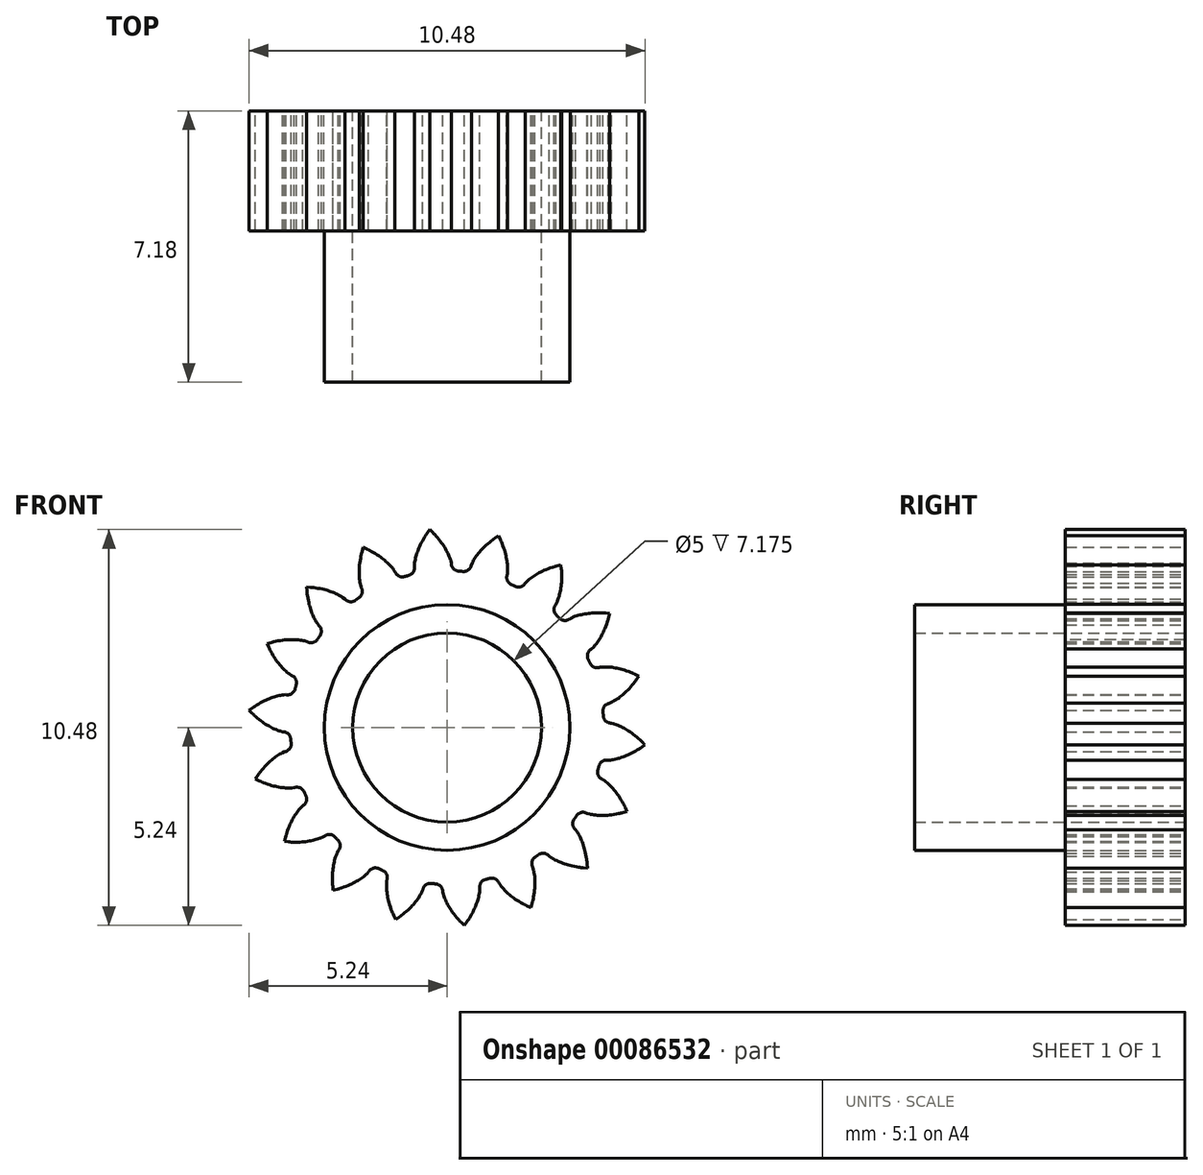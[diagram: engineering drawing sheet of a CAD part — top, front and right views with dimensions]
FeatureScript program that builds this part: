
annotation { "Feature Type Name" : "Feature", "Feature Type Description" : "" }
export const myFeature = defineFeature(function(context is Context, id is Id, definition is map)
    precondition{}
    {
        {
            assignVariable(context, id + "F0", {"name" : "Teeth", "anyValue" : 18});
        }
        {
            var Q0;
            Q0=qCreatedBy(makeId("Front.planeOp"),FACE);
            var sketch = newSketch(context, id + "F1", { "sketchPlane" : qUnion([Q0])});
            skCircle(sketch, "E0", {"center": v(0, 0) * mm, "radius": 4.24 * mm, "construction": true});
            skLineSegment(sketch, "E1", {"start": v(0, 0) * mm, "end": v(-0.2, 4.24) * mm, "construction": true});
            skLineSegment(sketch, "E2", {"start": v(0, 0) * mm, "end": v(-0.52, 4.21) * mm, "construction": true});
            skLineSegment(sketch, "E3", {"start": v(0, 0) * mm, "end": v(-0.84, 4.16) * mm, "construction": true});
            skLineSegment(sketch, "E4", {"start": v(-0.84, 4.16) * mm, "end": v(0.11, 4.35) * mm, "construction": true});
            skLineSegment(sketch, "E5", {"start": v(0, 0) * mm, "end": v(-1.15, 4.08) * mm, "construction": true});
            skLineSegment(sketch, "E6", {"start": v(-1.15, 4.08) * mm, "end": v(0.1, 4.43) * mm, "construction": true});
            skLineSegment(sketch, "E7", {"start": v(-0.84, 4.16) * mm, "end": v(-0.52, 4.21) * mm, "construction": true});
            skLineSegment(sketch, "E8", {"start": v(-1.15, 4.08) * mm, "end": v(-0.84, 4.16) * mm, "construction": true});
            skLineSegment(sketch, "E9", {"start": v(-0.84, 4.16) * mm, "end": v(-0.2, 4.24) * mm, "construction": true});
            skLineSegment(sketch, "E10", {"start": v(-1.15, 4.08) * mm, "end": v(-0.2, 4.24) * mm, "construction": true});
            skLineSegment(sketch, "E11", {"start": v(0, 0) * mm, "end": v(-2.05, 3.72) * mm, "construction": true});
            skLineSegment(sketch, "E12", {"start": v(-2.05, 3.72) * mm, "end": v(-0.09, 4.8) * mm, "construction": true});
            skLineSegment(sketch, "E13", {"start": v(0, 0) * mm, "end": v(-1.76, 3.86) * mm, "construction": true});
            skLineSegment(sketch, "E14", {"start": v(-1.76, 3.86) * mm, "end": v(0, 4.66) * mm, "construction": true});
            skLineSegment(sketch, "E15", {"start": v(0, 0) * mm, "end": v(-1.46, 3.98) * mm, "construction": true});
            skLineSegment(sketch, "E16", {"start": v(-1.46, 3.98) * mm, "end": v(0.05, 4.54) * mm, "construction": true});
            skLineSegment(sketch, "E17", {"start": v(-1.46, 3.98) * mm, "end": v(-1.15, 4.08) * mm, "construction": true});
            skLineSegment(sketch, "E18", {"start": v(-1.46, 3.98) * mm, "end": v(-1.76, 3.86) * mm, "construction": true});
            skLineSegment(sketch, "E19", {"start": v(-1.76, 3.86) * mm, "end": v(-2.05, 3.72) * mm, "construction": true});
            skLineSegment(sketch, "E20", {"start": v(-1.46, 3.98) * mm, "end": v(-0.2, 4.24) * mm, "construction": true});
            skLineSegment(sketch, "E21", {"start": v(-1.76, 3.86) * mm, "end": v(-0.2, 4.24) * mm, "construction": true});
            skLineSegment(sketch, "E22", {"start": v(-2.05, 3.72) * mm, "end": v(-0.2, 4.24) * mm, "construction": true});
            skLineSegment(sketch, "E23", {"start": v(0, 0) * mm, "end": v(-2.59, 3.36) * mm, "construction": true});
            skLineSegment(sketch, "E24", {"start": v(-2.59, 3.36) * mm, "end": v(-0.32, 5.1) * mm, "construction": true});
            skLineSegment(sketch, "E25", {"start": v(0, 0) * mm, "end": v(-2.84, 3.15) * mm, "construction": true});
            skLineSegment(sketch, "E26", {"start": v(-2.84, 3.15) * mm, "end": v(-0.49, 5.27) * mm, "construction": true});
            skLineSegment(sketch, "E27", {"start": v(0, 0) * mm, "end": v(-3.07, 2.93) * mm, "construction": true});
            skLineSegment(sketch, "E28", {"start": v(0, 0) * mm, "end": v(-2.33, 3.55) * mm, "construction": true});
            skLineSegment(sketch, "E29", {"start": v(-2.33, 3.55) * mm, "end": v(-0.2, 4.95) * mm, "construction": true});
            skLineSegment(sketch, "E30", {"start": v(-2.05, 3.72) * mm, "end": v(-2.33, 3.55) * mm, "construction": true});
            skLineSegment(sketch, "E31", {"start": v(-2.33, 3.55) * mm, "end": v(-2.59, 3.36) * mm, "construction": true});
            skLineSegment(sketch, "E32", {"start": v(-2.59, 3.36) * mm, "end": v(-2.84, 3.15) * mm, "construction": true});
            skLineSegment(sketch, "E33", {"start": v(-2.84, 3.15) * mm, "end": v(-3.07, 2.93) * mm, "construction": true});
            skLineSegment(sketch, "E34", {"start": v(-0.2, 4.24) * mm, "end": v(-2.33, 3.55) * mm, "construction": true});
            skLineSegment(sketch, "E35", {"start": v(-0.2, 4.24) * mm, "end": v(-2.59, 3.36) * mm, "construction": true});
            skLineSegment(sketch, "E36", {"start": v(-0.2, 4.24) * mm, "end": v(-2.84, 3.15) * mm, "construction": true});
            skLineSegment(sketch, "E37", {"start": v(-0.2, 4.24) * mm, "end": v(-3.07, 2.93) * mm, "construction": true});
            skCircle(sketch, "E38", {"center": v(0, 0) * mm, "radius": 4.76 * mm, "construction": true});
            skCircle(sketch, "E39", {"center": v(0, 0) * mm, "radius": 5.3 * mm});
            skPoint(sketch, "E40", {"position": v(0, 4.76) * mm});
            skLineSegment(sketch, "E41", {"start": v(0, 0) * mm, "end": v(-0.75, 8.57) * mm, "construction": true});
            skPoint(sketch, "E42.MirrorP", {"position": v(-0.83, 4.7) * mm});
            skLineSegment(sketch, "E43", {"start": v(-0.83, 4.7) * mm, "end": v(0, 0) * mm, "construction": true});
            skLineSegment(sketch, "E44", {"start": v(0, 0) * mm, "end": v(0, 4.76) * mm, "construction": true});
            skLineSegment(sketch, "E45", {"start": v(-0.52, 4.21) * mm, "end": v(-0.2, 4.24) * mm, "construction": true});
            skLineSegment(sketch, "E46", {"start": v(0.11, 4.35) * mm, "end": v(0.1, 4.43) * mm, "construction": true});
            skLineSegment(sketch, "E47", {"start": v(0, 0) * mm, "end": v(0, 10.19) * mm, "construction": true});
            skCircle(sketch, "E48", {"center": v(0, 0) * mm, "radius": 4.15 * mm});
            skSolve(sketch);
        }
        {
            var Q0;
            Q0=qCreatedBy(makeId("Front.planeOp"),FACE);
            var sketch = newSketch(context, id + "F2", { "sketchPlane" : qUnion([Q0])});
            skCircle(sketch, "E49.0", {"center": v(0, 0) * mm, "radius": 4.76 * mm, "construction": true});
            skPoint(sketch, "E50.0", {"position": v(-0.49, 5.27) * mm});
            skPoint(sketch, "E50.1", {"position": v(-0.32, 5.1) * mm});
            skPoint(sketch, "E50.2", {"position": v(-0.2, 4.95) * mm});
            skPoint(sketch, "E50.3", {"position": v(-0.09, 4.8) * mm});
            skPoint(sketch, "E50.4", {"position": v(0, 4.66) * mm});
            skPoint(sketch, "E50.6", {"position": v(0.1, 4.43) * mm});
            skPoint(sketch, "E50.7", {"position": v(0.11, 4.35) * mm});
            skPoint(sketch, "E50.8", {"position": v(0.05, 4.54) * mm});
            skLineSegment(sketch, "E51.0", {"start": v(0, 0) * mm, "end": v(-0.75, 8.57) * mm, "construction": true});
            skFitSpline(sketch, "E52", {"points": [v(-0.49, 5.27) * mm, v(-0.32, 5.1) * mm, v(-0.2, 4.95) * mm, v(-0.09, 4.8) * mm, v(0, 4.66) * mm, v(0.05, 4.54) * mm, v(0.1, 4.43) * mm, v(0.11, 4.35) * mm], "startDerivative": vector(2.81, -2.8) * mm, "endDerivative": vector(0.65, -2.34) * mm});
            skFitSpline(sketch, "E53.MirrorCS", {"points": [v(-0.43, 5.27) * mm, v(-0.57, 5.09) * mm, v(-0.67, 4.9) * mm, v(-0.75, 4.74) * mm, v(-0.8, 4.6) * mm, v(-0.84, 4.46) * mm, v(-0.86, 4.35) * mm, v(-0.87, 4.27) * mm], "startDerivative": vector(-2.28, -3.25) * mm, "endDerivative": vector(-0.24, -2.42) * mm});
            skCircle(sketch, "E54", {"center": v(0, 0) * mm, "radius": 2.5 * mm});
            skCircle(sketch, "E55.0", {"center": v(0, 0) * mm, "radius": 4.15 * mm});
            skArc(sketch, "E56", {"start": v(-0.49, 5.27) * mm, "mid": v(0.46, -5.27) * mm, "end": v(-0.43, 5.27) * mm});
            skLineSegment(sketch, "E57", {"start": v(-0.87, 4.27) * mm, "end": v(0, 0) * mm});
            skLineSegment(sketch, "E58", {"start": v(0, 0) * mm, "end": v(0.11, 4.35) * mm});
            skSolve(sketch);
        }
        {
            var Q0;
            {var subQ1=sQuery(id+"F2.wireOp",EDGE,"E52");var subQ9=sQuery(id+"F2.wireOp",EDGE,"rA0usyOi-Jm6w-jZNR-JSDv-ujEcH4bsm2Ol");var subQ11=makeQuery(id+"F2.imprint","INTERSECT",VERTEX,{"derivedFrom":[subQ1,subQ9]});Q0=makeQuery(id+"F2.imprint","IMPRINT",FACE,{"disambiguationData":[TD([[makeQuery(id+"F2.imprint","IMPRINT",EDGE,{"disambiguationData":[TD([[subQ11,1.0]])],"derivedFrom":subQ1}),-1.0]])]});}
            var Q1;
            {var subQ0=sQuery(id+"F2.wireOp",EDGE,"QqPcIgQ4-TZE6-73E5-WQaq-ugCT5JtziKyn");var subQ1=sQuery(id+"F2.wireOp",EDGE,"90be38e0-c88f-493d-85a8-1201295b9109.0");var subQ2=makeQuery(id+"F2.imprint","INTERSECT",VERTEX,{"derivedFrom":[subQ1,subQ0]});Q1=makeQuery(id+"F2.imprint","IMPRINT",FACE,{"disambiguationData":[TD([[makeQuery(id+"F2.imprint","IMPRINT",EDGE,{"disambiguationData":[TD([[subQ2,1.0]])],"derivedFrom":subQ1}),1.0]])]});}
            var Q2;
            {var subQ0=sQuery(id+"F2.wireOp",EDGE,"QqPcIgQ4-TZE6-73E5-WQaq-ugCT5JtziKyn");var subQ1=sQuery(id+"F2.wireOp",EDGE,"90be38e0-c88f-493d-85a8-1201295b9109.0");var subQ2=makeQuery(id+"F2.imprint","INTERSECT",VERTEX,{"derivedFrom":[subQ1,subQ0]});Q2=makeQuery(id+"F2.imprint","IMPRINT",FACE,{"disambiguationData":[TD([[makeQuery(id+"F2.imprint","IMPRINT",EDGE,{"disambiguationData":[TD([[subQ2,-1.0]])],"derivedFrom":subQ1}),1.0]])]});}
            var Q3;
            {var subQ1=sQuery(id+"F2.wireOp",EDGE,"E52");var subQ8=sQuery(id+"F2.wireOp",EDGE,"b861a5ab-cd51-40f1-92ab-cea0f5fe0d4d.1");var subQ11=makeQuery(id+"F2.imprint","INTERSECT",VERTEX,{"derivedFrom":[subQ1,subQ8]});Q3=makeQuery(id+"F2.imprint","IMPRINT",FACE,{"disambiguationData":[TD([[makeQuery(id+"F2.imprint","IMPRINT",EDGE,{"disambiguationData":[TD([[subQ11,1.0]])],"derivedFrom":subQ1}),-1.0]])]});}
            var Q4;
            {var subQ0=sQuery(id+"F2.wireOp",EDGE,"b861a5ab-cd51-40f1-92ab-cea0f5fe0d4d.0");var subQ1=sQuery(id+"F2.wireOp",EDGE,"E54");var subQ2=makeQuery(id+"F2.imprint","INTERSECT",VERTEX,{"derivedFrom":[subQ1,subQ0]});Q4=makeQuery(id+"F2.imprint","IMPRINT",FACE,{"disambiguationData":[TD([[makeQuery(id+"F2.imprint","IMPRINT",EDGE,{"disambiguationData":[TD([[subQ2,-1.0]])],"derivedFrom":subQ1}),-1.0]])]});}
            var Q5;
            {var subQ0=sQuery(id+"F2.wireOp",EDGE,"b861a5ab-cd51-40f1-92ab-cea0f5fe0d4d.0");var subQ1=sQuery(id+"F2.wireOp",EDGE,"E54");var subQ2=makeQuery(id+"F2.imprint","INTERSECT",VERTEX,{"derivedFrom":[subQ1,subQ0]});Q5=makeQuery(id+"F2.imprint","IMPRINT",FACE,{"disambiguationData":[TD([[makeQuery(id+"F2.imprint","IMPRINT",EDGE,{"disambiguationData":[TD([[subQ2,1.0]])],"derivedFrom":subQ1}),-1.0]])]});}
            extrude(context, id + "F3", {"entities" : qUnion([Q0, Q1, Q2, Q3, Q4, Q5]), "depth" : 3.17 * mm});
        }
        {
            var Q0;
            Q0=makeQuery(id+"F3.opExtrude","SWEPT_EDGE",EDGE,{"disambiguationData":[OSD([sQuery(id+"F2.wireOp",EDGE,"b861a5ab-cd51-40f1-92ab-cea0f5fe0d4d.1"),sQuery(id+"F2.wireOp",EDGE,"E55.0")])]});
            var Q1;
            Q1=makeQuery(id+"F3.opExtrude","SWEPT_EDGE",EDGE,{"disambiguationData":[OSD([sQuery(id+"F2.wireOp",EDGE,"b861a5ab-cd51-40f1-92ab-cea0f5fe0d4d.0"),sQuery(id+"F2.wireOp",EDGE,"E55.0")])]});
            fillet(context, id + "F4", {"entities" : qUnion([Q0, Q1]), "radius" : 0.2 * mm, "tangentPropagation" : true, "allowEdgeOverflow" : false});
        }
        {
            var Q0;
            Q0=makeQuery(id+"F4.opFillet","BLEND_FACE",FACE,{"disambiguationData":[OSD([sQuery(id+"F2.wireOp",EDGE,"E55.0"),sQuery(id+"F2.wireOp",EDGE,"E57")])]});
            var Q1;
            Q1=makeQuery(id+"F3.opExtrude","SWEPT_FACE",FACE,{"disambiguationData":[OSD([sQuery(id+"F2.wireOp",EDGE,"E57")])]});
            var Q2;
            Q2=makeQuery(id+"F3.opExtrude","SWEPT_FACE",FACE,{"disambiguationData":[OSD([sQuery(id+"F2.wireOp",EDGE,"E53.MirrorCS")])]});
            var Q3;
            Q3=makeQuery(id+"F3.opExtrude","SWEPT_FACE",FACE,{"disambiguationData":[OSD([sQuery(id+"F2.wireOp",EDGE,"E56")])]});
            var Q4;
            Q4=makeQuery(id+"F3.opExtrude","SWEPT_FACE",FACE,{"disambiguationData":[OSD([sQuery(id+"F2.wireOp",EDGE,"E52")])]});
            var Q5;
            Q5=makeQuery(id+"F3.opExtrude","SWEPT_FACE",FACE,{"disambiguationData":[OSD([sQuery(id+"F2.wireOp",EDGE,"E58")])]});
            var Q6;
            Q6=makeQuery(id+"F4.opFillet","BLEND_FACE",FACE,{"disambiguationData":[OSD([sQuery(id+"F2.wireOp",EDGE,"E55.0"),sQuery(id+"F2.wireOp",EDGE,"E58")])]});
            var Q7;
            Q7=makeQuery(id+"F3.opExtrude","SWEPT_FACE",FACE,{"disambiguationData":[OSD([sQuery(id+"F2.wireOp",EDGE,"E55.0")])]});
            circularPattern(context, id + "F5", {"faces" : qUnion([Q0, Q1, Q2, Q3, Q4, Q5, Q6]), "axis" : qUnion([Q7]), "angle" : 360 * degree, "instanceCount" : round(getVariable(context, 'Teeth')), "equalSpace" : true, "patternType" : PatternType.FACE});
        }
        {
            var Q0;
            Q0=makeQuery(id+"F3.opExtrude","CAP_FACE",FACE,{"disambiguationData":[OSD([sQuery(id+"F2.wireOp",EDGE,"E52"),sQuery(id+"F2.wireOp",EDGE,"E53.MirrorCS"),sQuery(id+"F2.wireOp",EDGE,"E54"),sQuery(id+"F2.wireOp",EDGE,"E55.0"),sQuery(id+"F2.wireOp",EDGE,"E57"),sQuery(id+"F2.wireOp",EDGE,"E58")])],"isStart":false});
            var sketch = newSketch(context, id + "F6", { "sketchPlane" : qUnion([Q0])});
            skCircle(sketch, "E59", {"center": v(0, 0) * mm, "radius": 3.25 * mm});
            skSolve(sketch);
        }
        {
            var Q0;
            Q0=makeQuery(id+"F6.imprint","IMPRINT",FACE,{"disambiguationData":[TD([[makeQuery(id+"F6.imprint","IMPRINT",EDGE,{"derivedFrom":sQuery(id+"F6.wireOp",EDGE,"E59")}),1.0]])]});
            extrude(context, id + "F7", {"entities" : qUnion([Q0]), "operationType" : NewBodyOperationType.ADD, "depth" : 4 * mm});
        }
    });
